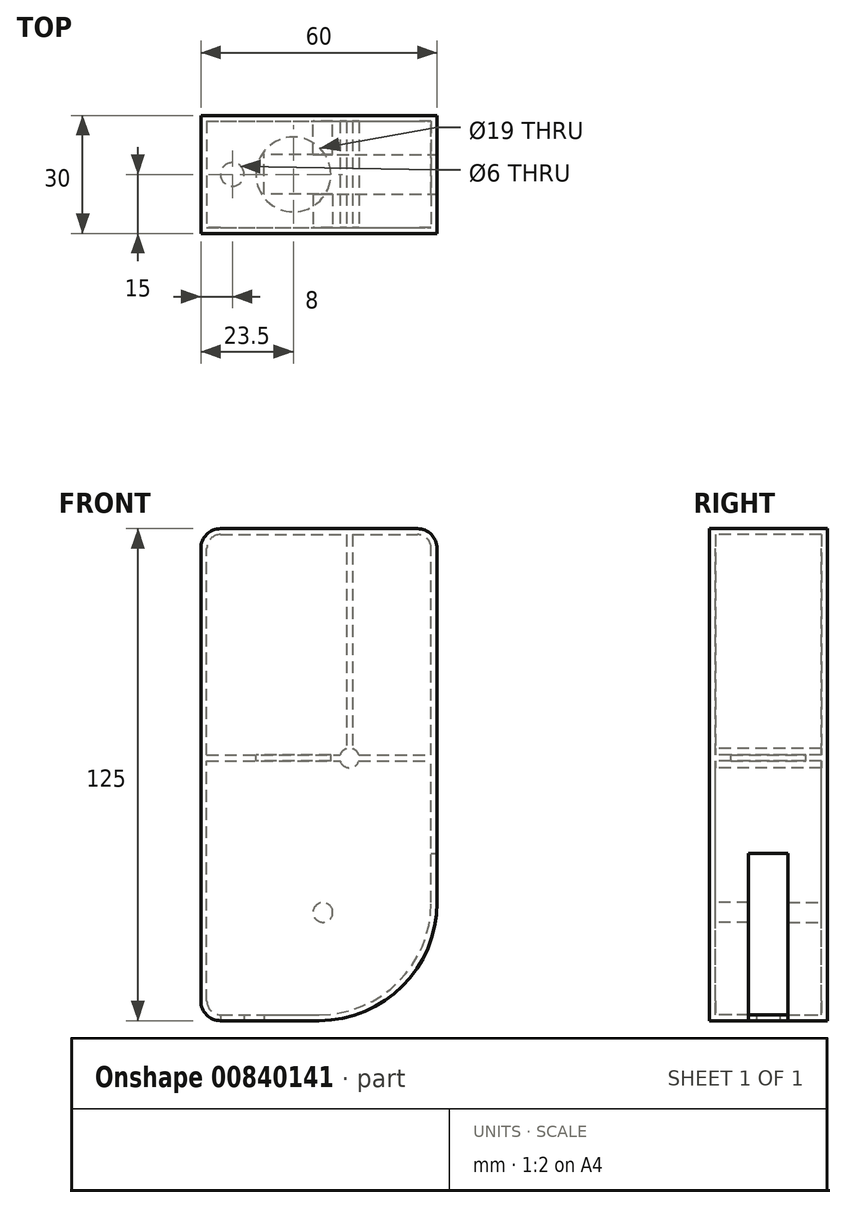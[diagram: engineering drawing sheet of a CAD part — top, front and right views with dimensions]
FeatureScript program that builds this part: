
annotation { "Feature Type Name" : "Feature", "Feature Type Description" : "" }
export const myFeature = defineFeature(function(context is Context, id is Id, definition is map)
    precondition{}
    {
        {
            var Q0;
            Q0=qCreatedBy(makeId("Front.planeOp"),FACE);
            var sketch = newSketch(context, id + "F0", { "sketchPlane" : qUnion([Q0])});
            skLineSegment(sketch, "E0.bottom", {"start": v(0, 0) * mm, "end": v(60, 0) * mm});
            skLineSegment(sketch, "E0.top", {"start": v(0, 125) * mm, "end": v(60, 125) * mm});
            skLineSegment(sketch, "E0.left", {"start": v(0, 0) * mm, "end": v(0, 125) * mm});
            skLineSegment(sketch, "E0.right", {"start": v(60, 0) * mm, "end": v(60, 125) * mm});
            skSolve(sketch);
        }
        {
            var Q0;
            Q0=makeQuery(id+"F0.imprint","IMPRINT",FACE,{"disambiguationData":[TD([[makeQuery(id+"F0.imprint","IMPRINT",EDGE,{"derivedFrom":sQuery(id+"F0.wireOp",EDGE,"E0.bottom")}),1.0]])]});
            extrude(context, id + "F1", {"entities" : qUnion([Q0]), "depth" : 15 * mm, "offsetDistance" : 25 * mm});
        }
        {
            var Q0;
            Q0=makeQuery(id+"F1.opExtrude","SWEPT_EDGE",EDGE,{"disambiguationData":[OSD([sQuery(id+"F0.wireOp",EDGE,"E0.top"),sQuery(id+"F0.wireOp",EDGE,"E0.left")])]});
            var Q1;
            Q1=makeQuery(id+"F1.opExtrude","SWEPT_EDGE",EDGE,{"disambiguationData":[OSD([sQuery(id+"F0.wireOp",EDGE,"E0.top"),sQuery(id+"F0.wireOp",EDGE,"E0.right")])]});
            var Q2;
            Q2=makeQuery(id+"F1.opExtrude","SWEPT_EDGE",EDGE,{"disambiguationData":[OSD([sQuery(id+"F0.wireOp",EDGE,"E0.bottom"),sQuery(id+"F0.wireOp",EDGE,"E0.left")])]});
            fillet(context, id + "F2", {"entities" : qUnion([Q0, Q1, Q2]), "radius" : 5 * mm, "tangentPropagation" : true, "allowEdgeOverflow" : false});
        }
        {
            var Q0;
            Q0=makeQuery(id+"F1.opExtrude","SWEPT_EDGE",EDGE,{"disambiguationData":[OSD([sQuery(id+"F0.wireOp",EDGE,"E0.bottom"),sQuery(id+"F0.wireOp",EDGE,"E0.right")])]});
            fillet(context, id + "F3", {"entities" : qUnion([Q0]), "radius" : 30 * mm, "tangentPropagation" : true, "allowEdgeOverflow" : false});
        }
        {
            var Q0;
            Q0=makeQuery(id+"F1.opExtrude","CAP_FACE",FACE,{"disambiguationData":[OSD([sQuery(id+"F0.wireOp",EDGE,"E0.bottom"),sQuery(id+"F0.wireOp",EDGE,"E0.top"),sQuery(id+"F0.wireOp",EDGE,"E0.left"),sQuery(id+"F0.wireOp",EDGE,"E0.right")])],"isStart":false});
            shell(context, id + "F4", {"entities" : qUnion([Q0]), "thickness" : 1.5 * mm});
        }
        {
            var Q0;
            Q0=makeQuery(id+"F4.opShell","OFFSET_FACE",FACE,{"disambiguationData":[OSD([sQuery(id+"F0.wireOp",EDGE,"E0.bottom"),sQuery(id+"F0.wireOp",EDGE,"E0.top"),sQuery(id+"F0.wireOp",EDGE,"E0.left"),sQuery(id+"F0.wireOp",EDGE,"E0.right")])]});
            var sketch = newSketch(context, id + "F5", { "sketchPlane" : qUnion([Q0])});
            skLineSegment(sketch, "E1", {"start": v(1.5, 67.5) * mm, "end": v(58.5, 67.5) * mm});
            skLineSegment(sketch, "E2", {"start": v(1.5, 66) * mm, "end": v(58.5, 66) * mm});
            skSolve(sketch);
        }
        {
            var Q0;
            {var subQ0=sQuery(id+"F5.wireOp",EDGE,"E1");Q0=makeQuery(id+"F5.imprint","IMPRINT",FACE,{"disambiguationData":[TD([[makeQuery(id+"F5.imprint","IMPRINT",EDGE,{"derivedFrom":subQ0}),-1.0]])]});}
            var Q1;
            Q1=makeQuery(id+"F1.opExtrude","CAP_FACE",FACE,{"disambiguationData":[OSD([sQuery(id+"F0.wireOp",EDGE,"E0.bottom"),sQuery(id+"F0.wireOp",EDGE,"E0.top"),sQuery(id+"F0.wireOp",EDGE,"E0.left"),sQuery(id+"F0.wireOp",EDGE,"E0.right")])],"isStart":false});
            extrude(context, id + "F6", {"entities" : qUnion([Q0]), "operationType" : NewBodyOperationType.ADD, "endBound" : BoundingType.UP_TO_SURFACE, "depth" : 25 * mm, "endBoundEntityFace" : qUnion([Q1]), "offsetDistance" : 25 * mm});
        }
        {
            var Q0;
            Q0=makeQuery(id+"F6.opExtrude","SWEPT_FACE",FACE,{"disambiguationData":[OSD([sQuery(id+"F5.wireOp",EDGE,"E1")])]});
            var sketch = newSketch(context, id + "F7", { "sketchPlane" : qUnion([Q0])});
            skCircle(sketch, "E3", {"center": v(23.5, -15) * mm, "radius": 9.5 * mm});
            skSolve(sketch);
        }
        {
            var Q0;
            Q0 = qSketchRegion(id + "F7", true);
            var Q1;
            Q1=makeQuery(id+"F6.opExtrude","SWEPT_FACE",FACE,{"disambiguationData":[OSD([sQuery(id+"F5.wireOp",EDGE,"E2")])]});
            extrude(context, id + "F8", {"entities" : qUnion([Q0]), "operationType" : NewBodyOperationType.REMOVE, "endBound" : BoundingType.UP_TO_SURFACE, "oppositeDirection" : true, "depth" : 25 * mm, "endBoundEntityFace" : qUnion([Q1]), "offsetDistance" : 25 * mm});
        }
        {
            var Q0;
            {var subQ0=sQuery(id+"F0.wireOp",EDGE,"E0.left");var subQ1=sQuery(id+"F0.wireOp",EDGE,"E0.top");var subQ2=sQuery(id+"F0.wireOp",EDGE,"E0.right");Q0=makeQuery(id+"F6.boolean.opBoolean","SPLIT",FACE,{"disambiguationData":[TD([makeQuery(id+"F4.opShell","OFFSET_FACE",FACE,{"disambiguationData":[OSD([subQ1])]})])],"derivedFrom":makeQuery(id+"F4.opShell","OFFSET_FACE",FACE,{"disambiguationData":[OSD([sQuery(id+"F0.wireOp",EDGE,"E0.bottom"),subQ1,subQ0,subQ2])]})});}
            var sketch = newSketch(context, id + "F9", { "sketchPlane" : qUnion([Q0])});
            skLineSegment(sketch, "E4", {"start": v(37, 123.5) * mm, "end": v(37, 67.5) * mm});
            skLineSegment(sketch, "E5", {"start": v(38.5, 123.5) * mm, "end": v(38.5, 67.5) * mm});
            skSolve(sketch);
        }
        {
            var Q0;
            {var subQ0=sQuery(id+"F9.wireOp",EDGE,"E4");Q0=makeQuery(id+"F9.imprint","IMPRINT",FACE,{"disambiguationData":[TD([[makeQuery(id+"F9.imprint","IMPRINT",EDGE,{"derivedFrom":subQ0}),1.0]])]});}
            var Q1;
            {var subQ0=sQuery(id+"F0.wireOp",EDGE,"E0.right");var subQ1=sQuery(id+"F0.wireOp",EDGE,"E0.left");Q1=makeQuery(id+"F6.boolean.opBoolean","MERGE",FACE,{"derivedFrom":[makeQuery(id+"F1.opExtrude","CAP_FACE",FACE,{"disambiguationData":[OSD([sQuery(id+"F0.wireOp",EDGE,"E0.bottom"),sQuery(id+"F0.wireOp",EDGE,"E0.top"),subQ1,subQ0])],"isStart":false}),makeQuery(id+"F6.opExtrude","CAP_FACE",FACE,{"disambiguationData":[OSD([subQ1,subQ0,sQuery(id+"F5.wireOp",EDGE,"E1"),sQuery(id+"F5.wireOp",EDGE,"E2")])],"isStart":false})]});}
            extrude(context, id + "F10", {"entities" : qUnion([Q0]), "operationType" : NewBodyOperationType.ADD, "endBound" : BoundingType.UP_TO_SURFACE, "depth" : 25 * mm, "endBoundEntityFace" : qUnion([Q1]), "offsetDistance" : 25 * mm});
        }
        {
            var Q0;
            {var subQ0=sQuery(id+"F0.wireOp",EDGE,"E0.left");var subQ1=makeQuery(id+"F4.opShell","OFFSET_FACE",FACE,{"disambiguationData":[OSD([subQ0])]});var subQ3=sQuery(id+"F0.wireOp",EDGE,"E0.top");var subQ5=makeQuery(id+"F4.opShell","OFFSET_FACE",FACE,{"disambiguationData":[OSD([subQ3])]});var subQ6=sQuery(id+"F0.wireOp",EDGE,"E0.right");Q0=makeQuery(id+"F10.boolean.opBoolean","SPLIT",FACE,{"disambiguationData":[TD([subQ1])],"derivedFrom":makeQuery(id+"F6.boolean.opBoolean","SPLIT",FACE,{"disambiguationData":[TD([subQ5])],"derivedFrom":makeQuery(id+"F4.opShell","OFFSET_FACE",FACE,{"disambiguationData":[OSD([sQuery(id+"F0.wireOp",EDGE,"E0.bottom"),subQ3,subQ0,subQ6])]})})});}
            var sketch = newSketch(context, id + "F11", { "sketchPlane" : qUnion([Q0])});
            skLineSegment(sketch, "E6.bottom", {"start": v(37, 67.5) * mm, "end": v(38.5, 67.5) * mm, "construction": true});
            skLineSegment(sketch, "E6.top", {"start": v(37, 66) * mm, "end": v(38.5, 66) * mm, "construction": true});
            skLineSegment(sketch, "E6.left", {"start": v(37, 67.5) * mm, "end": v(37, 66) * mm, "construction": true});
            skLineSegment(sketch, "E6.right", {"start": v(38.5, 67.5) * mm, "end": v(38.5, 66) * mm, "construction": true});
            skLineSegment(sketch, "E7", {"start": v(37, 67.5) * mm, "end": v(38.5, 66) * mm, "construction": true});
            skLineSegment(sketch, "E8", {"start": v(38.5, 67.5) * mm, "end": v(37, 66) * mm});
            skCircle(sketch, "E9", {"center": v(37.75, 66.75) * mm, "radius": 2.5 * mm});
            skSolve(sketch);
        }
        {
            var Q0;
            Q0 = qSketchRegion(id + "F11", true);
            var Q1;
            {var subQ0=sQuery(id+"F5.wireOp",EDGE,"E1");var subQ1=sQuery(id+"F0.wireOp",EDGE,"E0.top");var subQ2=sQuery(id+"F0.wireOp",EDGE,"E0.right");var subQ3=sQuery(id+"F0.wireOp",EDGE,"E0.left");Q1=makeQuery(id+"F10.boolean.opBoolean","MERGE",FACE,{"derivedFrom":[makeQuery(id+"F6.boolean.opBoolean","MERGE",FACE,{"derivedFrom":[makeQuery(id+"F1.opExtrude","CAP_FACE",FACE,{"disambiguationData":[OSD([sQuery(id+"F0.wireOp",EDGE,"E0.bottom"),subQ1,subQ3,subQ2])],"isStart":false}),makeQuery(id+"F6.opExtrude","CAP_FACE",FACE,{"disambiguationData":[OSD([subQ3,subQ2,subQ0,sQuery(id+"F5.wireOp",EDGE,"E2")])],"isStart":false})]}),makeQuery(id+"F10.opExtrude","CAP_FACE",FACE,{"disambiguationData":[OSD([subQ1,subQ0,sQuery(id+"F9.wireOp",EDGE,"E4"),sQuery(id+"F9.wireOp",EDGE,"E5")])],"isStart":false})]});}
            extrude(context, id + "F12", {"entities" : qUnion([Q0]), "operationType" : NewBodyOperationType.ADD, "endBound" : BoundingType.UP_TO_SURFACE, "depth" : 25 * mm, "endBoundEntityFace" : qUnion([Q1]), "offsetDistance" : 25 * mm});
        }
        {
            var Q0;
            Q0=makeQuery(id+"F1.opExtrude","SWEPT_FACE",FACE,{"disambiguationData":[OSD([sQuery(id+"F0.wireOp",EDGE,"E0.bottom")])]});
            var sketch = newSketch(context, id + "F13", { "sketchPlane" : qUnion([Q0])});
            skCircle(sketch, "E10", {"center": v(8, 15) * mm, "radius": 3 * mm});
            skSolve(sketch);
        }
        {
            var Q0;
            {var subQ0=sQuery(id+"F13.wireOp",EDGE,"E10");var subQ1=sQuery(id+"F0.wireOp",EDGE,"E0.bottom");var subQ2=makeQuery(id+"F1.opExtrude","CAP_EDGE",EDGE,{"disambiguationData":[OSD([subQ1])],"isStart":false});var subQ4=makeQuery(id+"F13.imprint","INTERSECT",VERTEX,{"derivedFrom":[subQ2,subQ0]});Q0=makeQuery(id+"F13.imprint","IMPRINT",FACE,{"disambiguationData":[TD([[makeQuery(id+"F13.imprint","IMPRINT",EDGE,{"disambiguationData":[TD([[subQ4,-1.0]])],"derivedFrom":subQ0}),1.0]])]});}
            var Q1;
            {var subQ0=sQuery(id+"F13.wireOp",EDGE,"E10");var subQ1=sQuery(id+"F0.wireOp",EDGE,"E0.bottom");var subQ2=makeQuery(id+"F1.opExtrude","CAP_EDGE",EDGE,{"disambiguationData":[OSD([subQ1])],"isStart":false});var subQ4=makeQuery(id+"F13.imprint","INTERSECT",VERTEX,{"derivedFrom":[subQ2,subQ0]});Q1=makeQuery(id+"F13.imprint","IMPRINT",FACE,{"disambiguationData":[TD([[makeQuery(id+"F13.imprint","IMPRINT",EDGE,{"disambiguationData":[TD([[subQ4,1.0]])],"derivedFrom":subQ0}),1.0]])]});}
            var Q2;
            Q2=sQuery(id+"F13.wireOp",EDGE,"E10");
            var Q3;
            Q3=makeQuery(id+"F4.opShell","OFFSET_FACE",FACE,{"disambiguationData":[OSD([sQuery(id+"F0.wireOp",EDGE,"E0.bottom")])]});
            extrude(context, id + "F14", {"entities" : qUnion([Q0, Q1]), "operationType" : NewBodyOperationType.REMOVE, "surfaceEntities" : qUnion([Q2]), "endBound" : BoundingType.UP_TO_SURFACE, "oppositeDirection" : true, "depth" : 25 * mm, "endBoundEntityFace" : qUnion([Q3]), "offsetDistance" : 25 * mm});
        }
        {
            var Q0;
            {var subQ0=sQuery(id+"F0.wireOp",EDGE,"E0.bottom");var subQ1=sQuery(id+"F0.wireOp",EDGE,"E0.left");var subQ2=sQuery(id+"F0.wireOp",EDGE,"E0.right");Q0=makeQuery(id+"F6.boolean.opBoolean","SPLIT",FACE,{"disambiguationData":[TD([makeQuery(id+"F4.opShell","OFFSET_FACE",FACE,{"disambiguationData":[OSD([subQ0])]})])],"derivedFrom":makeQuery(id+"F4.opShell","OFFSET_FACE",FACE,{"disambiguationData":[OSD([subQ0,sQuery(id+"F0.wireOp",EDGE,"E0.top"),subQ1,subQ2])]})});}
            var sketch = newSketch(context, id + "F15", { "sketchPlane" : qUnion([Q0])});
            skCircle(sketch, "E11", {"center": v(31, 27.5) * mm, "radius": 2.5 * mm});
            skSolve(sketch);
        }
        {
            var Q0;
            Q0=makeQuery(id+"F15.imprint","IMPRINT",FACE,{"disambiguationData":[TD([[makeQuery(id+"F15.imprint","IMPRINT",EDGE,{"derivedFrom":sQuery(id+"F15.wireOp",EDGE,"E11")}),1.0]])]});
            var Q1;
            {var subQ0=sQuery(id+"F5.wireOp",EDGE,"E1");var subQ1=sQuery(id+"F0.wireOp",EDGE,"E0.top");var subQ2=sQuery(id+"F0.wireOp",EDGE,"E0.right");var subQ3=sQuery(id+"F0.wireOp",EDGE,"E0.left");Q1=makeQuery(id+"F12.boolean.opBoolean","MERGE",FACE,{"derivedFrom":[makeQuery(id+"F10.boolean.opBoolean","MERGE",FACE,{"derivedFrom":[makeQuery(id+"F6.boolean.opBoolean","MERGE",FACE,{"derivedFrom":[makeQuery(id+"F1.opExtrude","CAP_FACE",FACE,{"disambiguationData":[OSD([sQuery(id+"F0.wireOp",EDGE,"E0.bottom"),subQ1,subQ3,subQ2])],"isStart":false}),makeQuery(id+"F6.opExtrude","CAP_FACE",FACE,{"disambiguationData":[OSD([subQ3,subQ2,subQ0,sQuery(id+"F5.wireOp",EDGE,"E2")])],"isStart":false})]}),makeQuery(id+"F10.opExtrude","CAP_FACE",FACE,{"disambiguationData":[OSD([subQ1,subQ0,sQuery(id+"F9.wireOp",EDGE,"E4"),sQuery(id+"F9.wireOp",EDGE,"E5")])],"isStart":false})]}),makeQuery(id+"F12.opExtrude","CAP_FACE",FACE,{"disambiguationData":[OSD([sQuery(id+"F11.wireOp",EDGE,"E9")])],"isStart":false})]});}
            extrude(context, id + "F16", {"entities" : qUnion([Q0]), "operationType" : NewBodyOperationType.ADD, "endBound" : BoundingType.UP_TO_SURFACE, "depth" : 25 * mm, "endBoundEntityFace" : qUnion([Q1]), "offsetDistance" : 25 * mm});
        }
        {
            var Q0;
            {var subQ0=sQuery(id+"F5.wireOp",EDGE,"E1");var subQ1=sQuery(id+"F0.wireOp",EDGE,"E0.top");var subQ2=sQuery(id+"F0.wireOp",EDGE,"E0.right");var subQ3=sQuery(id+"F0.wireOp",EDGE,"E0.left");Q0=makeQuery(id+"F12.boolean.opBoolean","MERGE",FACE,{"derivedFrom":[makeQuery(id+"F10.boolean.opBoolean","MERGE",FACE,{"derivedFrom":[makeQuery(id+"F6.boolean.opBoolean","MERGE",FACE,{"derivedFrom":[makeQuery(id+"F1.opExtrude","CAP_FACE",FACE,{"disambiguationData":[OSD([sQuery(id+"F0.wireOp",EDGE,"E0.bottom"),subQ1,subQ3,subQ2])],"isStart":false}),makeQuery(id+"F6.opExtrude","CAP_FACE",FACE,{"disambiguationData":[OSD([subQ3,subQ2,subQ0,sQuery(id+"F5.wireOp",EDGE,"E2")])],"isStart":false})]}),makeQuery(id+"F10.opExtrude","CAP_FACE",FACE,{"disambiguationData":[OSD([subQ1,subQ0,sQuery(id+"F9.wireOp",EDGE,"E4"),sQuery(id+"F9.wireOp",EDGE,"E5")])],"isStart":false})]}),makeQuery(id+"F12.opExtrude","CAP_FACE",FACE,{"disambiguationData":[OSD([sQuery(id+"F11.wireOp",EDGE,"E9")])],"isStart":false})]});}
            var sketch = newSketch(context, id + "F17", { "sketchPlane" : qUnion([Q0])});
            skCircle(sketch, "E12", {"center": v(31, 27.5) * mm, "radius": 15 * mm, "construction": true});
            skLineSegment(sketch, "E13", {"start": v(31, 42.5) * mm, "end": v(60, 42.5) * mm});
            skLineSegment(sketch, "E14", {"start": v(16, 27.5) * mm, "end": v(16, 0) * mm});
            skLineSegment(sketch, "E15", {"start": v(60, 42.5) * mm, "end": v(60, 0) * mm});
            skLineSegment(sketch, "E16", {"start": v(60, 0) * mm, "end": v(16, 0) * mm});
            skArc(sketch, "E17", {"start": v(31, 42.5) * mm, "mid": v(20.4, 38.1) * mm, "end": v(16, 27.5) * mm});
            skSolve(sketch);
        }
        {
            var Q0;
            Q0 = qSketchRegion(id + "F17", true);
            extrude(context, id + "F18", {"entities" : qUnion([Q0]), "operationType" : NewBodyOperationType.REMOVE, "oppositeDirection" : true, "depth" : 5 * mm, "offsetDistance" : 25 * mm});
        }
        {
            var Q0;
            Q0=makeQuery(id+"F1.opExtrude","SWEPT_BODY",BODY,{"disambiguationData":[OSD([sQuery(id+"F0.wireOp",EDGE,"E0.bottom"),sQuery(id+"F0.wireOp",EDGE,"E0.top"),sQuery(id+"F0.wireOp",EDGE,"E0.left"),sQuery(id+"F0.wireOp",EDGE,"E0.right")])]});
            var Q1;
            {var subQ0=sQuery(id+"F0.wireOp",EDGE,"E0.left");var subQ1=sQuery(id+"F0.wireOp",EDGE,"E0.top");var subQ2=sQuery(id+"F0.wireOp",EDGE,"E0.right");var subQ3=sQuery(id+"F0.wireOp",EDGE,"E0.bottom");var subQ4=sQuery(id+"F5.wireOp",EDGE,"E2");var subQ5=sQuery(id+"F9.wireOp",EDGE,"E4");var subQ6=sQuery(id+"F5.wireOp",EDGE,"E1");var subQ7=sQuery(id+"F9.wireOp",EDGE,"E5");var subQ8=sQuery(id+"F11.wireOp",EDGE,"E9");Q1=makeQuery(id+"F18.boolean.opBoolean","SPLIT",FACE,{"disambiguationData":[TD([makeQuery(id+"F1.opExtrude","SWEPT_FACE",FACE,{"disambiguationData":[OSD([subQ1])]})])],"derivedFrom":makeQuery(id+"F12.boolean.opBoolean","MERGE",FACE,{"derivedFrom":[makeQuery(id+"F10.boolean.opBoolean","MERGE",FACE,{"derivedFrom":[makeQuery(id+"F6.boolean.opBoolean","MERGE",FACE,{"derivedFrom":[makeQuery(id+"F1.opExtrude","CAP_FACE",FACE,{"disambiguationData":[OSD([subQ3,subQ1,subQ0,subQ2])],"isStart":false}),makeQuery(id+"F6.opExtrude","CAP_FACE",FACE,{"disambiguationData":[OSD([subQ0,subQ2,subQ6,subQ4])],"isStart":false})]}),makeQuery(id+"F10.opExtrude","CAP_FACE",FACE,{"disambiguationData":[OSD([subQ1,subQ6,subQ5,subQ7])],"isStart":false})]}),makeQuery(id+"F12.opExtrude","CAP_FACE",FACE,{"disambiguationData":[OSD([subQ8])],"isStart":false})]})});}
            mirror(context, id + "F19", {"entities" : qUnion([Q0]), "mirrorPlane" : qUnion([Q1])});
        }
        {
            var Q0;
            Q0=makeQuery(id+"F1.opExtrude","SWEPT_BODY",BODY,{"disambiguationData":[OSD([sQuery(id+"F0.wireOp",EDGE,"E0.bottom"),sQuery(id+"F0.wireOp",EDGE,"E0.top"),sQuery(id+"F0.wireOp",EDGE,"E0.left"),sQuery(id+"F0.wireOp",EDGE,"E0.right")])]});
            var Q1;
            {var subQ0=sQuery(id+"F0.wireOp",EDGE,"E0.left");var subQ1=sQuery(id+"F0.wireOp",EDGE,"E0.top");var subQ2=sQuery(id+"F0.wireOp",EDGE,"E0.right");var subQ3=sQuery(id+"F0.wireOp",EDGE,"E0.bottom");var subQ4=sQuery(id+"F5.wireOp",EDGE,"E2");var subQ5=sQuery(id+"F9.wireOp",EDGE,"E4");var subQ6=sQuery(id+"F5.wireOp",EDGE,"E1");var subQ7=sQuery(id+"F9.wireOp",EDGE,"E5");var subQ8=sQuery(id+"F11.wireOp",EDGE,"E9");Q1=makeQuery(id+"F18.boolean.opBoolean","SPLIT",FACE,{"disambiguationData":[TD([makeQuery(id+"F1.opExtrude","SWEPT_FACE",FACE,{"disambiguationData":[OSD([subQ1])]})])],"derivedFrom":makeQuery(id+"F12.boolean.opBoolean","MERGE",FACE,{"derivedFrom":[makeQuery(id+"F10.boolean.opBoolean","MERGE",FACE,{"derivedFrom":[makeQuery(id+"F6.boolean.opBoolean","MERGE",FACE,{"derivedFrom":[makeQuery(id+"F1.opExtrude","CAP_FACE",FACE,{"disambiguationData":[OSD([subQ3,subQ1,subQ0,subQ2])],"isStart":false}),makeQuery(id+"F6.opExtrude","CAP_FACE",FACE,{"disambiguationData":[OSD([subQ0,subQ2,subQ6,subQ4])],"isStart":false})]}),makeQuery(id+"F10.opExtrude","CAP_FACE",FACE,{"disambiguationData":[OSD([subQ1,subQ6,subQ5,subQ7])],"isStart":false})]}),makeQuery(id+"F12.opExtrude","CAP_FACE",FACE,{"disambiguationData":[OSD([subQ8])],"isStart":false})]})});}
            mirror(context, id + "F20", {"operationType" : NewBodyOperationType.ADD, "entities" : qUnion([Q0]), "mirrorPlane" : qUnion([Q1])});
        }
    });
